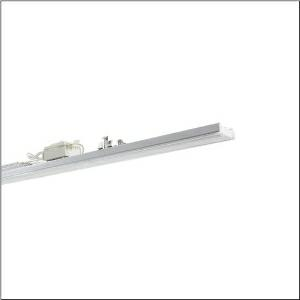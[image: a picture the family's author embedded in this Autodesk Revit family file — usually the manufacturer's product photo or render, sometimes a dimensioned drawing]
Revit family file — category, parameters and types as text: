
# Revit family: licross_21_recessed_mo_52tl12dv4dxg
name_source: partatom
category: Lighting Fixtures
units: mm (PartAtom-declared; Revit-internal decimal feet)

## family parameters
Cut with Voids When Loaded = No
Host = Face
Light Source = No
Part Type = Normal
Room Calculation Point = No
Round Connector Dimension = Use Diameter
Shared = No

## types (1)
- --- (1 x LED, 13000 lm, 71 W, 4000K)
    Apparent Load = 71 VA
    CIE Flux Codes = 72 92 99 100 100
    Color Rendering = 80
    Color Temperature = 4000K
    Default Elevation = 1800 mm
    Description = Licross 21 Recessed MO, luminaire insert, of sheet steel, galvanised, coil coated, white, length: 2.250mm, width: 66mm, height: 67mm, LED rated luminous flux: 13.000lm, light colour: 840, SDCM (Standard Deviation of Colour Matching)MacAdam ≤ 3 SDCM (initial), control gear: DALI 2, with plug, 5-pole, with phase selection, mains connection: 220..240V, AC, 50/60Hz, rated input power: 71W, internal wiring halogen-free, primary optical cover: cover, of PMMA, light emission: direct distribution, primary light characteristic: symmetric, protection rating (complete): IP40, insulation class (complete): insulation class I (protective earthing), certification: CE, ENEC, VDE, UKCA, protection symbol: D if used in an environment without relevant dust loads with corresponding accessories, impact resistance: IK06, permissible ambient temperature for indoor applications: -25..+35°C, corresponds to IFS (International Featured Standards) requirements for safety and quality in the food industry, reducing of maximum allowable ambient temperature of 5°C with ceiling mounting, LABS conformity tested according to VDMA 24364:2018-05, The light source and the operating device comply with the requirements of the Ecodesign Regulation (EU) 2019/2020 and are replaceable in accordance with this regulation, packaging unit: 1 piece
    Height = 58 mm
    Lamp = 1 x LED
    Lamp Light Flux = 13000 lm
    Lamp Power = 71 W
    Lamp count = 1
    Length = 2250 mm
    Luminous efficacy = 183 lm/W
    Manufacturer = Siteco
    ModVariant = No
    Model = 52TL12DV4DXG
    Mounting Place = Ceiling
    Mounting Type = Pendant
    Number of Poles = 1
    OnlyDefault = Yes
    Power Factor = 1
    Product Name = Licross 21 Recessed MO
    Product group = luminaire insert | ceiling pendant
    ProductGroupID = 901
    Protection Class = Protection class I
    Protection Degree = IP 40
    RLX_Detail_Level = 1
    RLX_Emergency_Light_Flux = 0 lm
    RLX_Emergency_Type = 0
    RLX_Emergency_Type_DB = No
    RlxData = <blob elided: 29917 chars, md5=a087f966>
    Socket = socket
    Standby Power = 0 W
    System Light Flux = 13000 lm
    System Power = 71 W
    Type Comments = factory setting: luminous flux: 100 % | dim-lin: 254 | 324 mA
    Type Image = l_1296930.jpg
    URL = http://relux.com
    VarID = @adj_126621
    Voltage = 0 V
    Weight = 0.00 kg
    Width = 66 mm

## geometry (parser evidence)
native form markers: Blend x4, Sweep x12
no freeform markers — native parametric forms only
